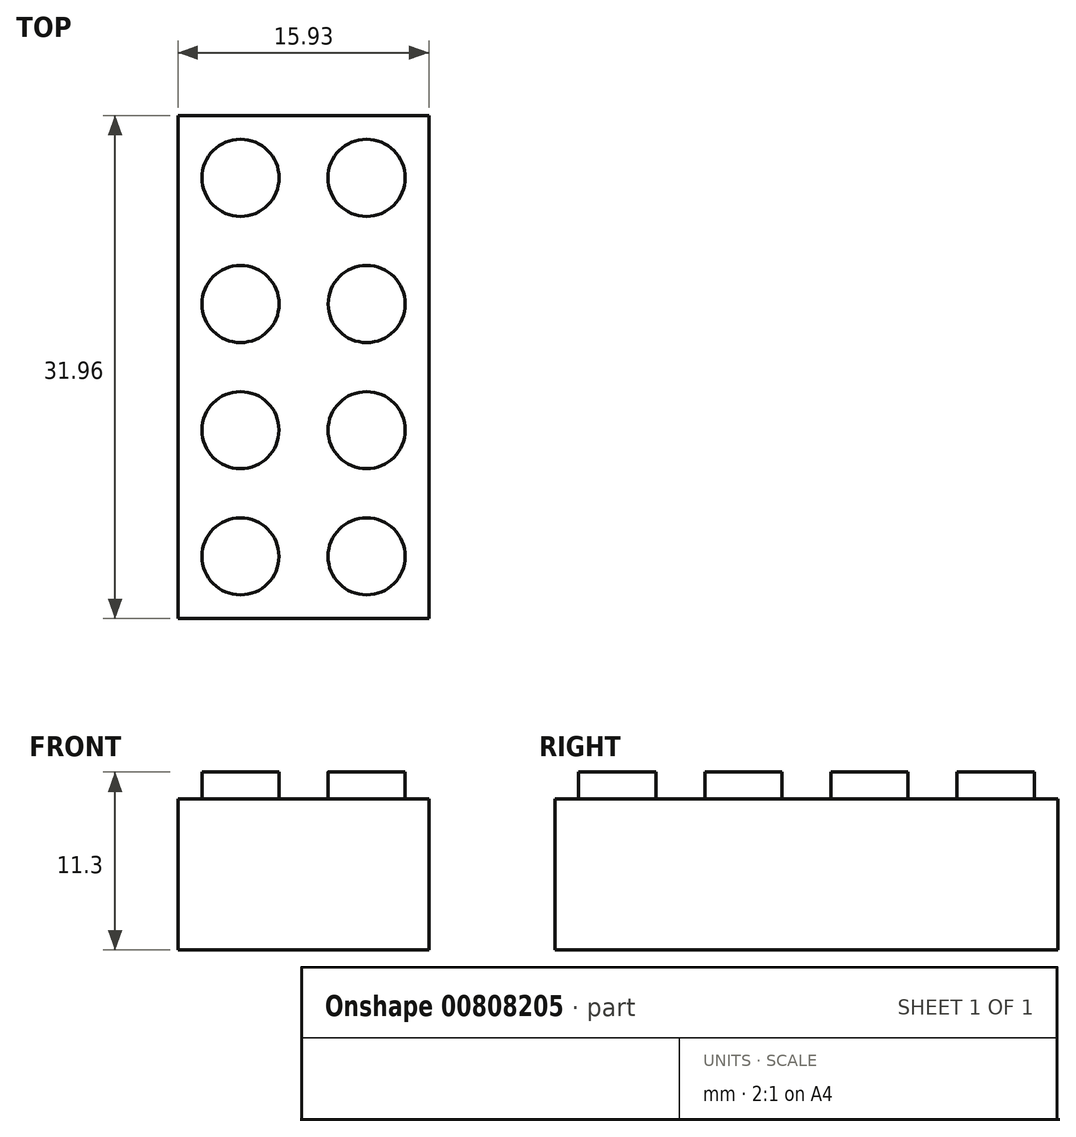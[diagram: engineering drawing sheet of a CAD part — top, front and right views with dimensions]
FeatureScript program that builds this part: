
annotation { "Feature Type Name" : "Feature", "Feature Type Description" : "" }
export const myFeature = defineFeature(function(context is Context, id is Id, definition is map)
    precondition{}
    {
        {
            var Q0;
            Q0=qCreatedBy(makeId("Top.planeOp"),FACE);
            var sketch = newSketch(context, id + "F0", { "sketchPlane" : qUnion([Q0])});
            skLineSegment(sketch, "E0", {"start": v(0, 0) * mm, "end": v(15.93, 0) * mm});
            skLineSegment(sketch, "E1", {"start": v(15.93, 0) * mm, "end": v(15.93, 31.96) * mm});
            skLineSegment(sketch, "E2", {"start": v(15.93, 31.96) * mm, "end": v(0, 31.96) * mm});
            skLineSegment(sketch, "E3", {"start": v(0, 31.96) * mm, "end": v(0, 0) * mm});
            skSolve(sketch);
        }
        {
            var Q0;
            Q0=makeQuery(id+"F0.imprint","IMPRINT",FACE,{"disambiguationData":[TD([[makeQuery(id+"F0.imprint","IMPRINT",EDGE,{"derivedFrom":sQuery(id+"F0.wireOp",EDGE,"E0")}),1.0]])]});
            extrude(context, id + "F1", {"entities" : qUnion([Q0]), "depth" : 9.6 * mm, "offsetDistance" : 25.4 * mm});
        }
        {
            var Q0;
            Q0=makeQuery(id+"F1.opExtrude","CAP_FACE",FACE,{"disambiguationData":[OSD([sQuery(id+"F0.wireOp",EDGE,"E0"),sQuery(id+"F0.wireOp",EDGE,"E1"),sQuery(id+"F0.wireOp",EDGE,"E2"),sQuery(id+"F0.wireOp",EDGE,"E3")])],"isStart":false});
            var sketch = newSketch(context, id + "F2", { "sketchPlane" : qUnion([Q0])});
            skLineSegment(sketch, "E4", {"start": v(0, 0) * mm, "end": v(3.96, 0) * mm, "construction": true});
            skLineSegment(sketch, "E5", {"start": v(3.96, 0) * mm, "end": v(3.96, 3.96) * mm, "construction": true});
            skCircle(sketch, "E6", {"center": v(3.96, 3.96) * mm, "radius": 2.45 * mm});
            skLineSegment(sketch, "E7", {"start": v(15.93, 0) * mm, "end": v(11.97, 0) * mm, "construction": true});
            skLineSegment(sketch, "E8", {"start": v(11.97, 0) * mm, "end": v(11.97, 3.96) * mm, "construction": true});
            skCircle(sketch, "E9", {"center": v(11.97, 3.96) * mm, "radius": 2.45 * mm});
            skLineSegment(sketch, "E10", {"start": v(15.93, 31.96) * mm, "end": v(11.97, 31.96) * mm, "construction": true});
            skLineSegment(sketch, "E11", {"start": v(0, 31.96) * mm, "end": v(3.96, 31.96) * mm, "construction": true});
            skLineSegment(sketch, "E12", {"start": v(3.96, 31.96) * mm, "end": v(3.96, 28) * mm, "construction": true});
            skCircle(sketch, "E13", {"center": v(3.96, 28) * mm, "radius": 2.45 * mm});
            skLineSegment(sketch, "E14", {"start": v(11.97, 31.96) * mm, "end": v(11.97, 28) * mm, "construction": true});
            skCircle(sketch, "E15", {"center": v(11.97, 28) * mm, "radius": 2.45 * mm});
            skLineSegment(sketch, "E16", {"start": v(3.96, 3.96) * mm, "end": v(3.96, 11.97) * mm, "construction": true});
            skCircle(sketch, "E17", {"center": v(3.96, 11.97) * mm, "radius": 2.45 * mm});
            skLineSegment(sketch, "E18", {"start": v(11.97, 3.96) * mm, "end": v(11.97, 11.97) * mm, "construction": true});
            skCircle(sketch, "E19", {"center": v(11.97, 11.97) * mm, "radius": 2.45 * mm});
            skLineSegment(sketch, "E20", {"start": v(3.96, 28) * mm, "end": v(3.96, 19.98) * mm, "construction": true});
            skCircle(sketch, "E21", {"center": v(3.96, 19.98) * mm, "radius": 2.45 * mm});
            skLineSegment(sketch, "E22", {"start": v(11.97, 28) * mm, "end": v(11.97, 23.1) * mm, "construction": true});
            skLineSegment(sketch, "E23", {"start": v(3.96, 19.98) * mm, "end": v(11.98, 19.98) * mm, "construction": true});
            skCircle(sketch, "E24", {"center": v(11.98, 19.98) * mm, "radius": 2.45 * mm});
            skSolve(sketch);
        }
        {
            var Q0;
            Q0=makeQuery(id+"F2.imprint","IMPRINT",FACE,{"disambiguationData":[TD([[makeQuery(id+"F2.imprint","IMPRINT",EDGE,{"derivedFrom":sQuery(id+"F2.wireOp",EDGE,"E9")}),1.0]])]});
            var Q1;
            Q1=makeQuery(id+"F2.imprint","IMPRINT",FACE,{"disambiguationData":[TD([[makeQuery(id+"F2.imprint","IMPRINT",EDGE,{"derivedFrom":sQuery(id+"F2.wireOp",EDGE,"E6")}),1.0]])]});
            var Q2;
            Q2=makeQuery(id+"F2.imprint","IMPRINT",FACE,{"disambiguationData":[TD([[makeQuery(id+"F2.imprint","IMPRINT",EDGE,{"derivedFrom":sQuery(id+"F2.wireOp",EDGE,"E15")}),1.0]])]});
            var Q3;
            Q3=makeQuery(id+"F2.imprint","IMPRINT",FACE,{"disambiguationData":[TD([[makeQuery(id+"F2.imprint","IMPRINT",EDGE,{"derivedFrom":sQuery(id+"F2.wireOp",EDGE,"E13")}),1.0]])]});
            var Q4;
            Q4=makeQuery(id+"F2.imprint","IMPRINT",FACE,{"disambiguationData":[TD([[makeQuery(id+"F2.imprint","IMPRINT",EDGE,{"derivedFrom":sQuery(id+"F2.wireOp",EDGE,"E21")}),1.0]])]});
            var Q5;
            Q5=makeQuery(id+"F2.imprint","IMPRINT",FACE,{"disambiguationData":[TD([[makeQuery(id+"F2.imprint","IMPRINT",EDGE,{"derivedFrom":sQuery(id+"F2.wireOp",EDGE,"E24")}),1.0]])]});
            var Q6;
            Q6=makeQuery(id+"F2.imprint","IMPRINT",FACE,{"disambiguationData":[TD([[makeQuery(id+"F2.imprint","IMPRINT",EDGE,{"derivedFrom":sQuery(id+"F2.wireOp",EDGE,"E19")}),1.0]])]});
            var Q7;
            Q7=makeQuery(id+"F2.imprint","IMPRINT",FACE,{"disambiguationData":[TD([[makeQuery(id+"F2.imprint","IMPRINT",EDGE,{"derivedFrom":sQuery(id+"F2.wireOp",EDGE,"E17")}),1.0]])]});
            extrude(context, id + "F3", {"entities" : qUnion([Q0, Q1, Q2, Q3, Q4, Q5, Q6, Q7]), "operationType" : NewBodyOperationType.ADD, "depth" : 1.7 * mm, "offsetDistance" : 25.4 * mm});
        }
    });
